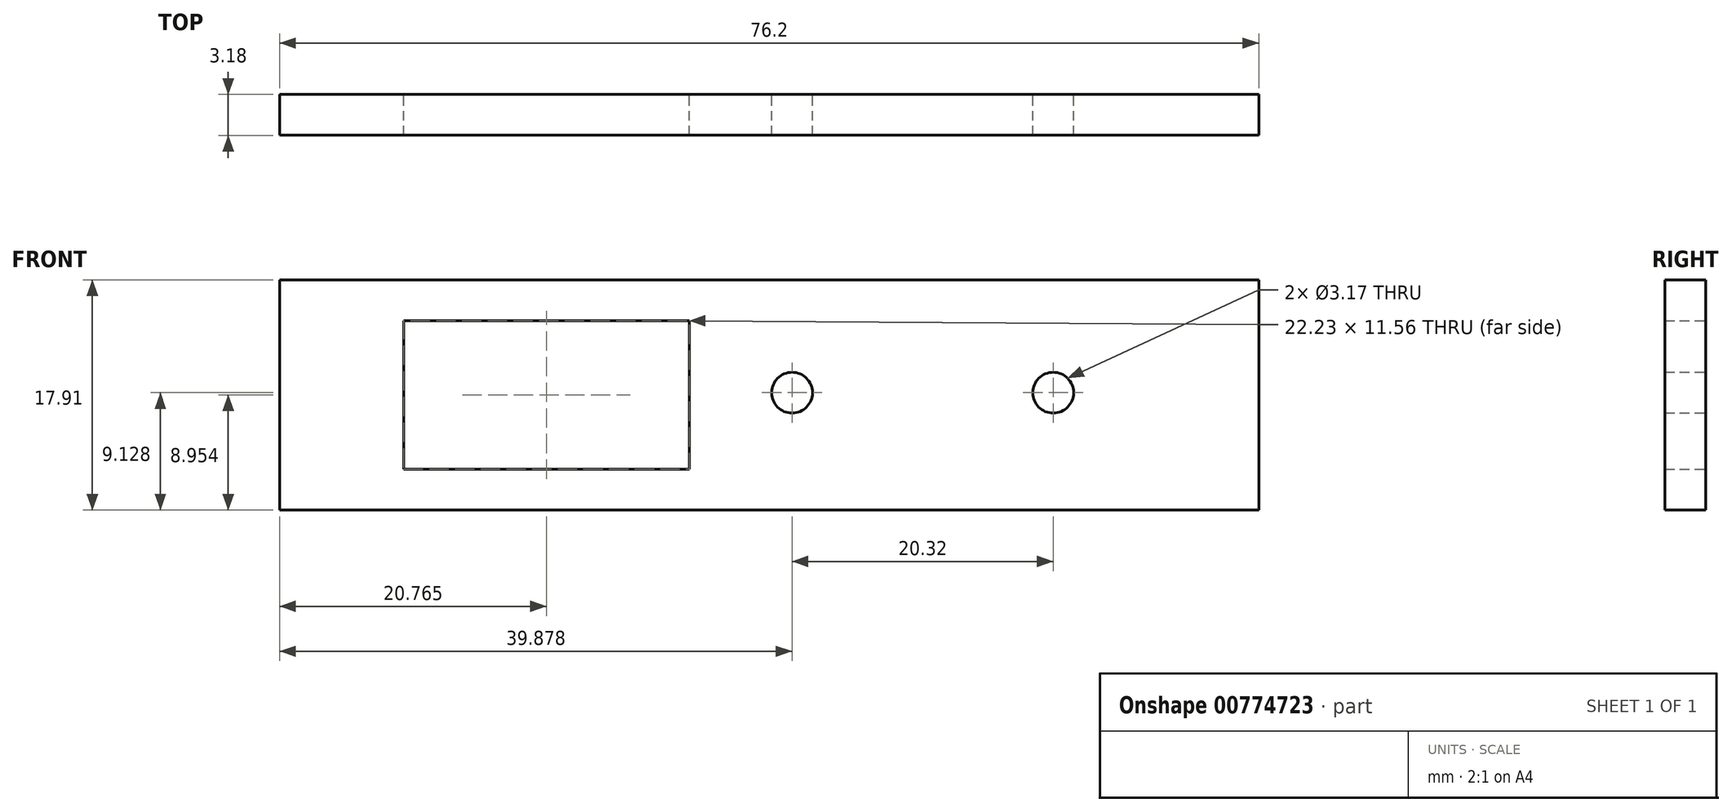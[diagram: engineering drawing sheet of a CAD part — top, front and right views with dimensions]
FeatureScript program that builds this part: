
annotation { "Feature Type Name" : "Feature", "Feature Type Description" : "" }
export const myFeature = defineFeature(function(context is Context, id is Id, definition is map)
    precondition{}
    {
        {
            var Q0;
            Q0=qCreatedBy(makeId("Front.planeOp"),FACE);
            var sketch = newSketch(context, id + "F0", { "sketchPlane" : qUnion([Q0])});
            skLineSegment(sketch, "E0", {"start": v(-38.1, 1.55) * mm, "end": v(38.1, 1.55) * mm});
            skLineSegment(sketch, "E1", {"start": v(-38.1, -16.36) * mm, "end": v(38.1, -16.36) * mm});
            skCircle(sketch, "E2", {"center": v(22.1, -7.23) * mm, "radius": 1.59 * mm});
            skCircle(sketch, "E3", {"center": v(1.78, -7.23) * mm, "radius": 1.59 * mm});
            skLineSegment(sketch, "E4", {"start": v(-38.1, 1.55) * mm, "end": v(-38.1, -16.36) * mm});
            skLineSegment(sketch, "E5", {"start": v(38.1, 1.55) * mm, "end": v(38.1, -16.36) * mm});
            skLineSegment(sketch, "E6", {"start": v(-38.1, -16.36) * mm, "end": v(-38.1, -13.18) * mm});
            skLineSegment(sketch, "E7", {"start": v(-38.1, 1.55) * mm, "end": v(-38.1, -1.63) * mm});
            skLineSegment(sketch, "E8", {"start": v(38.1, 1.55) * mm, "end": v(38.1, -1.63) * mm});
            skLineSegment(sketch, "E9", {"start": v(38.1, -16.36) * mm, "end": v(38.1, -13.18) * mm});
            skLineSegment(sketch, "E10", {"start": v(-28.45, -13.18) * mm, "end": v(-6.22, -13.18) * mm});
            skLineSegment(sketch, "E11", {"start": v(-28.45, -1.63) * mm, "end": v(-6.22, -1.63) * mm});
            skLineSegment(sketch, "E12", {"start": v(-6.22, -1.63) * mm, "end": v(-6.22, -13.18) * mm});
            skLineSegment(sketch, "E13", {"start": v(-28.45, -1.63) * mm, "end": v(-28.45, -13.18) * mm});
            skPoint(sketch, "E14.orphan", {"position": v(-6.22, -7.23) * mm});
            skPoint(sketch, "E15.orphan", {"position": v(-28.45, -7.23) * mm});
            skPoint(sketch, "E16.start.orphan", {"position": v(-22.1, -7.23) * mm});
            skSolve(sketch);
        }
        {
            var Q0;
            Q0=makeQuery(id+"F0.imprint","IMPRINT",FACE,{"disambiguationData":[TD([[makeQuery(id+"F0.imprint","IMPRINT",EDGE,{"derivedFrom":sQuery(id+"F0.wireOp",EDGE,"E0")}),-1.0]])]});
            extrude(context, id + "F1", {"entities" : qUnion([Q0]), "depth" : 3.17 * mm, "offsetDistance" : 25.4 * mm});
        }
    });
